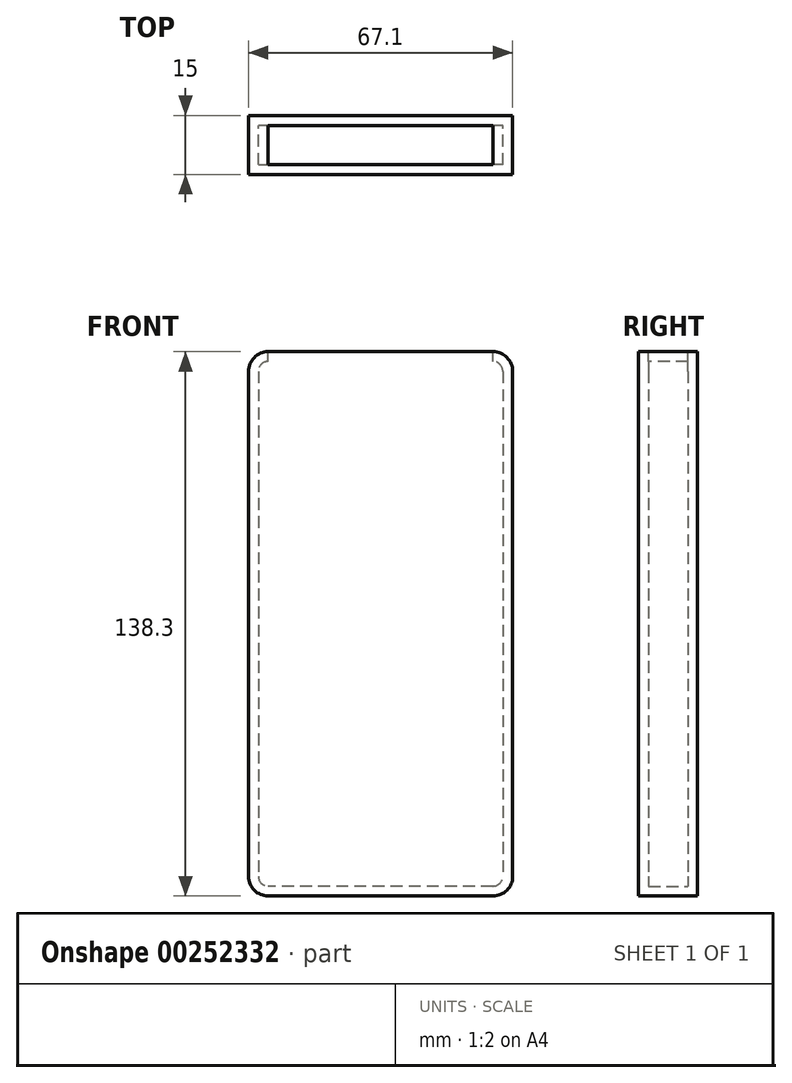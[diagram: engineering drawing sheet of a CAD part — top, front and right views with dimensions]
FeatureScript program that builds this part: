
annotation { "Feature Type Name" : "Feature", "Feature Type Description" : "" }
export const myFeature = defineFeature(function(context is Context, id is Id, definition is map)
    precondition{}
    {
        {
            var Q0;
            Q0=qCreatedBy(makeId("Front.planeOp"),FACE);
            var sketch = newSketch(context, id + "F0", { "sketchPlane" : qUnion([Q0])});
            skLineSegment(sketch, "E0.bottom", {"start": v(33.55, 69.15) * mm, "end": v(-33.55, 69.15) * mm});
            skLineSegment(sketch, "E0.top", {"start": v(33.55, -69.15) * mm, "end": v(-33.55, -69.15) * mm});
            skLineSegment(sketch, "E0.left", {"start": v(33.55, 69.15) * mm, "end": v(33.55, -69.15) * mm});
            skLineSegment(sketch, "E0.right", {"start": v(-33.55, 69.15) * mm, "end": v(-33.55, -69.15) * mm});
            skPoint(sketch, "E0.middle", {"position": v(0, 0) * mm});
            skSolve(sketch);
        }
        {
            var Q0;
            Q0=makeQuery(id+"F0.imprint","IMPRINT",FACE,{"disambiguationData":[TD([[makeQuery(id+"F0.imprint","IMPRINT",EDGE,{"derivedFrom":sQuery(id+"F0.wireOp",EDGE,"E0.bottom")}),1.0]])]});
            extrude(context, id + "F1", {"entities" : qUnion([Q0]), "oppositeDirection" : true, "depth" : 15 * mm});
        }
        {
            var Q0;
            Q0=makeQuery(id+"F1.opExtrude","SWEPT_EDGE",EDGE,{"disambiguationData":[OSD([sQuery(id+"F0.wireOp",EDGE,"E0.bottom"),sQuery(id+"F0.wireOp",EDGE,"E0.right")])]});
            var Q1;
            Q1=makeQuery(id+"F1.opExtrude","SWEPT_EDGE",EDGE,{"disambiguationData":[OSD([sQuery(id+"F0.wireOp",EDGE,"E0.bottom"),sQuery(id+"F0.wireOp",EDGE,"E0.left")])]});
            var Q2;
            Q2=makeQuery(id+"F1.opExtrude","SWEPT_EDGE",EDGE,{"disambiguationData":[OSD([sQuery(id+"F0.wireOp",EDGE,"E0.top"),sQuery(id+"F0.wireOp",EDGE,"E0.right")])]});
            var Q3;
            Q3=makeQuery(id+"F1.opExtrude","SWEPT_EDGE",EDGE,{"disambiguationData":[OSD([sQuery(id+"F0.wireOp",EDGE,"E0.top"),sQuery(id+"F0.wireOp",EDGE,"E0.left")])]});
            fillet(context, id + "F2", {"entities" : qUnion([Q0, Q1, Q2, Q3]), "radius" : 5 * mm, "tangentPropagation" : true, "allowEdgeOverflow" : false});
        }
        {
            var Q0;
            Q0=makeQuery(id+"F1.opExtrude","SWEPT_FACE",FACE,{"disambiguationData":[OSD([sQuery(id+"F0.wireOp",EDGE,"E0.bottom")])]});
            shell(context, id + "F3", {"entities" : qUnion([Q0]), "thickness" : 2.5 * mm});
        }
    });
